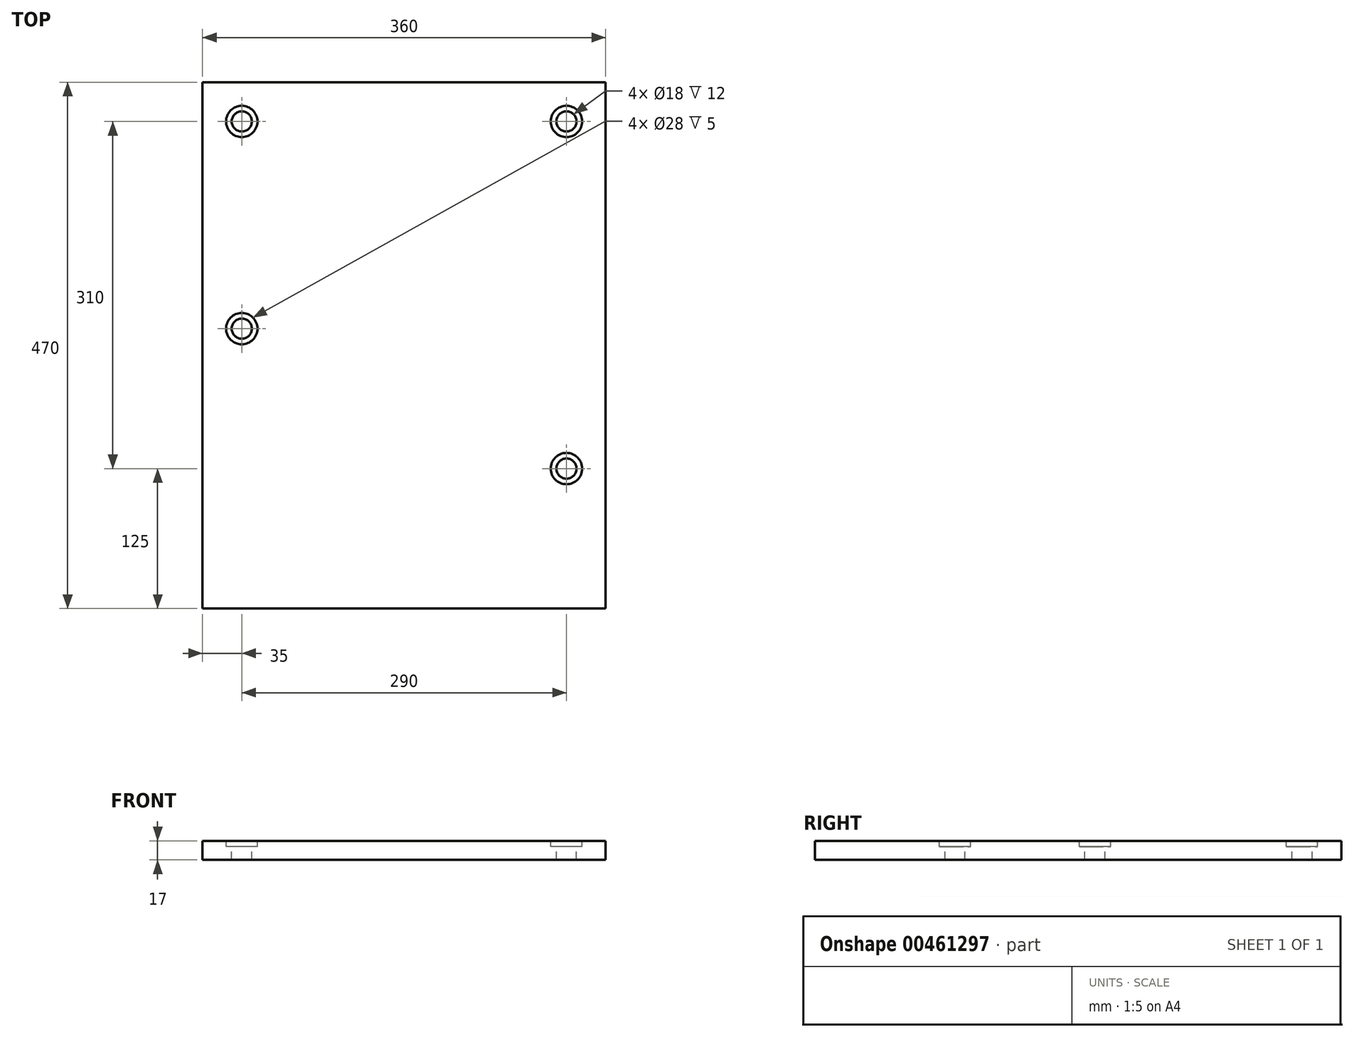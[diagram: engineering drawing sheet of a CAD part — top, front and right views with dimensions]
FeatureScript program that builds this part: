
annotation { "Feature Type Name" : "Feature", "Feature Type Description" : "" }
export const myFeature = defineFeature(function(context is Context, id is Id, definition is map)
    precondition{}
    {
        {
            var Q0;
            Q0=qCreatedBy(makeId("Top.planeOp"),FACE);
            var sketch = newSketch(context, id + "F0", { "sketchPlane" : qUnion([Q0])});
            skLineSegment(sketch, "E0.bottom", {"start": v(-360, 470) * mm, "end": v(0, 470) * mm});
            skLineSegment(sketch, "E0.top", {"start": v(-360, 0) * mm, "end": v(0, 0) * mm});
            skLineSegment(sketch, "E0.left", {"start": v(-360, 470) * mm, "end": v(-360, 0) * mm});
            skLineSegment(sketch, "E0.right", {"start": v(0, 470) * mm, "end": v(0, 0) * mm});
            skPoint(sketch, "E1", {"position": v(-180, 290) * mm});
            skPoint(sketch, "E2", {"position": v(-325, 435) * mm});
            skPoint(sketch, "E3", {"position": v(-35, 435) * mm});
            skPoint(sketch, "E4", {"position": v(-35, 125) * mm});
            skPoint(sketch, "E5", {"position": v(-325, 250) * mm});
            skSolve(sketch);
        }
        {
            var Q0;
            Q0 = qSketchRegion(id + "F0", true);
            extrude(context, id + "F1", {"entities" : qUnion([Q0]), "oppositeDirection" : true, "depth" : 17 * mm, "offsetDistance" : 25 * mm});
        }
        {
            var Q0;
            Q0=sQuery(id+"F0.wireOp",VERTEX,"E2");
            var Q1;
            Q1=sQuery(id+"F0.wireOp",VERTEX,"E5");
            var Q2;
            Q2=sQuery(id+"F0.wireOp",VERTEX,"E4");
            var Q3;
            Q3=sQuery(id+"F0.wireOp",VERTEX,"E3");
            var Q4;
            Q4=makeQuery(id+"F1.opExtrude","SWEPT_BODY",BODY,{"disambiguationData":[OSD([sQuery(id+"F0.wireOp",EDGE,"E0.bottom"),sQuery(id+"F0.wireOp",EDGE,"E0.top"),sQuery(id+"F0.wireOp",EDGE,"E0.left"),sQuery(id+"F0.wireOp",EDGE,"E0.right")])]});
            hole(context, id + "F2", {"style" : HoleStyle.C_BORE, "endStyle" : HoleEndStyle.THROUGH, "holeDiameter" : 18 * mm, "cBoreDiameter" : 28 * mm, "cBoreDepth" : 5 * mm, "majorDiameter" : 5 * mm, "isTappedThrough" : true, "tappedDepth" : 12 * mm, "tapClearance" : 3, "locations" : qUnion([Q0, Q1, Q2, Q3]), "scope" : qUnion([Q4])});
        }
    });
